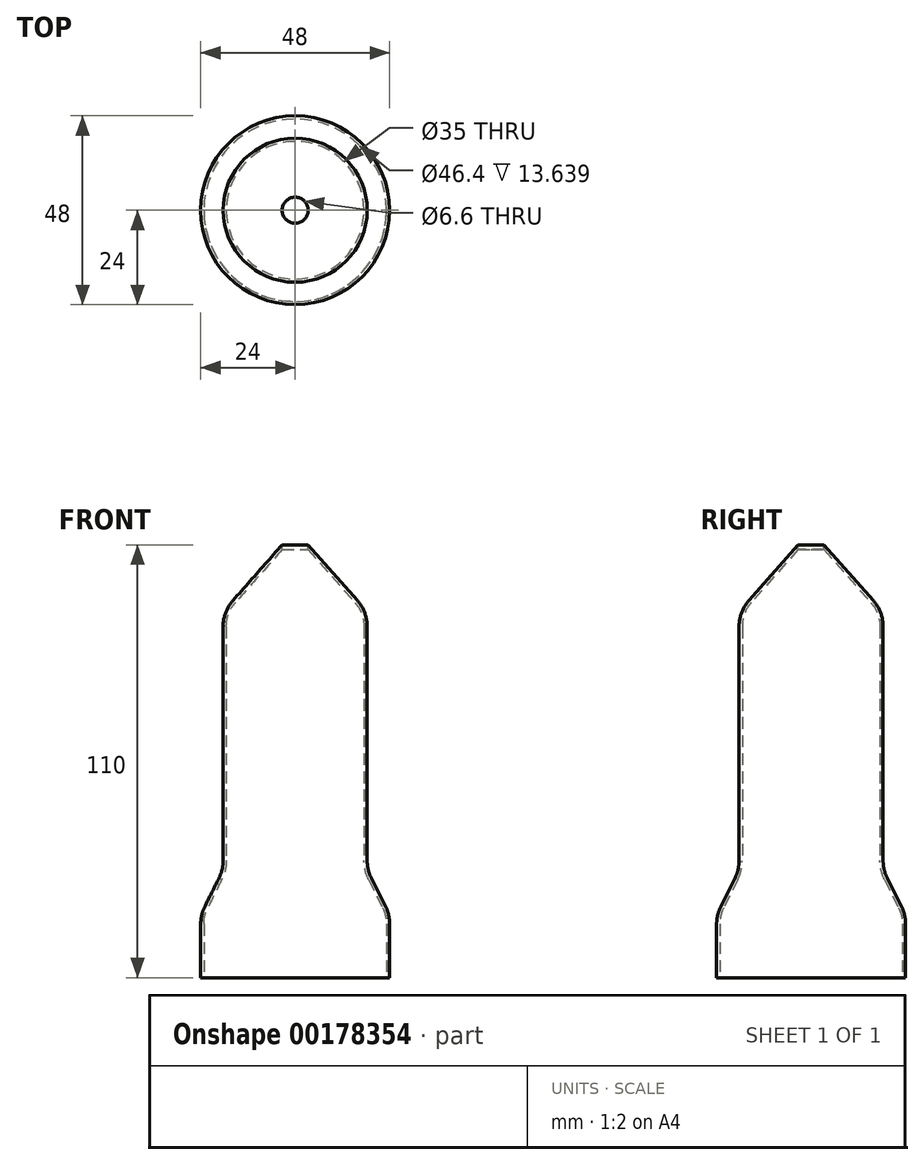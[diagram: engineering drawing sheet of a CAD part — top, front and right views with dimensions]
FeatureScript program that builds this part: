
annotation { "Feature Type Name" : "Feature", "Feature Type Description" : "" }
export const myFeature = defineFeature(function(context is Context, id is Id, definition is map)
    precondition{}
    {
        {
            var Q0;
            Q0=qCreatedBy(makeId("Top.planeOp"),FACE);
            var sketch = newSketch(context, id + "F0", { "sketchPlane" : qUnion([Q0])});
            skCircle(sketch, "E0", {"center": v(0, 0) * mm, "radius": 24 * mm});
            skLineSegment(sketch, "E1", {"start": v(0, 0) * mm, "end": v(0, 27.34) * mm, "construction": true});
            skCircle(sketch, "E2", {"center": v(0, 0) * mm, "radius": 18.3 * mm});
            skCircle(sketch, "E3", {"center": v(0, 0) * mm, "radius": 19.5 * mm});
            skSolve(sketch);
        }
        {
            var Q0;
            Q0=makeQuery(id+"F0.imprint","IMPRINT",FACE,{"disambiguationData":[TD([[makeQuery(id+"F0.imprint","IMPRINT",EDGE,{"derivedFrom":sQuery(id+"F0.wireOp",EDGE,"E2")}),1.0]])]});
            extrude(context, id + "F1", {"entities" : qUnion([Q0]), "depth" : 110 * mm});
        }
        {
            var Q0;
            Q0=makeQuery(id+"F0.imprint","IMPRINT",FACE,{"disambiguationData":[TD([[makeQuery(id+"F0.imprint","IMPRINT",EDGE,{"derivedFrom":sQuery(id+"F0.wireOp",EDGE,"E0")}),1.0]])]});
            var Q1;
            Q1=makeQuery(id+"F0.imprint","IMPRINT",FACE,{"disambiguationData":[TD([[makeQuery(id+"F0.imprint","IMPRINT",EDGE,{"derivedFrom":sQuery(id+"F0.wireOp",EDGE,"E2")}),-1.0]])]});
            extrude(context, id + "F2", {"entities" : qUnion([Q0, Q1]), "operationType" : NewBodyOperationType.ADD, "depth" : 30 * mm});
        }
        {
            var Q0;
            Q0=makeQuery(id+"F2.opExtrude","CAP_EDGE",EDGE,{"disambiguationData":[OSD([sQuery(id+"F0.wireOp",EDGE,"E0")])],"isStart":false});
            chamfer(context, id + "F3", {"entities" : qUnion([Q0]), "chamferType" : ChamferType.TWO_OFFSETS, "width1" : 7 * mm, "oppositeDirection" : false, "width2" : 14 * mm, "tangentPropagation" : true});
        }
        {
            var Q0;
            Q0=makeQuery(id+"F1.opExtrude","CAP_EDGE",EDGE,{"disambiguationData":[OSD([sQuery(id+"F0.wireOp",EDGE,"E2")])],"isStart":false});
            chamfer(context, id + "F4", {"entities" : qUnion([Q0]), "chamferType" : ChamferType.TWO_OFFSETS, "width1" : 15 * mm, "oppositeDirection" : false, "width2" : 17 * mm, "tangentPropagation" : true});
        }
        {
            var Q0;
            {var subQ0=sQuery(id+"F0.wireOp",EDGE,"E2");Q0=makeQuery(id+"F4.opChamfer","BLEND_EDGE",EDGE,{"blendedFrom":[makeQuery(id+"F1.opExtrude","CAP_EDGE",EDGE,{"disambiguationData":[OSD([subQ0])],"isStart":false}),makeQuery(id+"F1.opExtrude","SWEPT_FACE",FACE,{"disambiguationData":[OSD([subQ0])]})],"blendedInto":[makeQuery(id+"F1.opExtrude","SWEPT_FACE",FACE,{"disambiguationData":[OSD([subQ0])]})]});}
            var Q1;
            Q1=makeQuery(id+"F3.opChamfer","BLEND_EDGE",EDGE,{"blendedFrom":[makeQuery(id+"F2.opExtrude","CAP_EDGE",EDGE,{"disambiguationData":[OSD([sQuery(id+"F0.wireOp",EDGE,"E0")])],"isStart":false}),makeQuery(id+"F1.opExtrude","SWEPT_FACE",FACE,{"disambiguationData":[OSD([sQuery(id+"F0.wireOp",EDGE,"E2")])]})],"blendedInto":[makeQuery(id+"F1.opExtrude","SWEPT_FACE",FACE,{"disambiguationData":[OSD([sQuery(id+"F0.wireOp",EDGE,"E2")])]})]});
            var Q2;
            {var subQ0=sQuery(id+"F0.wireOp",EDGE,"E0");Q2=makeQuery(id+"F3.opChamfer","BLEND_EDGE",EDGE,{"blendedFrom":[makeQuery(id+"F2.opExtrude","CAP_EDGE",EDGE,{"disambiguationData":[OSD([subQ0])],"isStart":false}),makeQuery(id+"F2.opExtrude","SWEPT_FACE",FACE,{"disambiguationData":[OSD([subQ0])]})],"blendedInto":[makeQuery(id+"F2.opExtrude","SWEPT_FACE",FACE,{"disambiguationData":[OSD([subQ0])]})]});}
            fillet(context, id + "F5", {"entities" : qUnion([Q0, Q1, Q2]), "radius" : 10 * mm, "tangentPropagation" : true, "allowEdgeOverflow" : false});
        }
        {
            var Q0;
            {var subQ0=sQuery(id+"F0.wireOp",EDGE,"E2");Q0=makeQuery(id+"F2.boolean.opBoolean","MERGE",FACE,{"derivedFrom":[makeQuery(id+"F1.opExtrude","CAP_FACE",FACE,{"disambiguationData":[OSD([subQ0])],"isStart":true}),makeQuery(id+"F2.opExtrude","CAP_FACE",FACE,{"disambiguationData":[OSD([sQuery(id+"F0.wireOp",EDGE,"E0"),subQ0])],"isStart":true})]});}
            shell(context, id + "F6", {"entities" : qUnion([Q0]), "thickness" : 0.8 * mm});
        }
        {
            var Q0;
            Q0=makeQuery(id+"F1.opExtrude","CAP_FACE",FACE,{"disambiguationData":[OSD([sQuery(id+"F0.wireOp",EDGE,"E2")])],"isStart":false});
            extrude(context, id + "F7", {"entities" : qUnion([Q0]), "operationType" : NewBodyOperationType.REMOVE, "oppositeDirection" : true, "depth" : 25 * mm});
        }
    });
